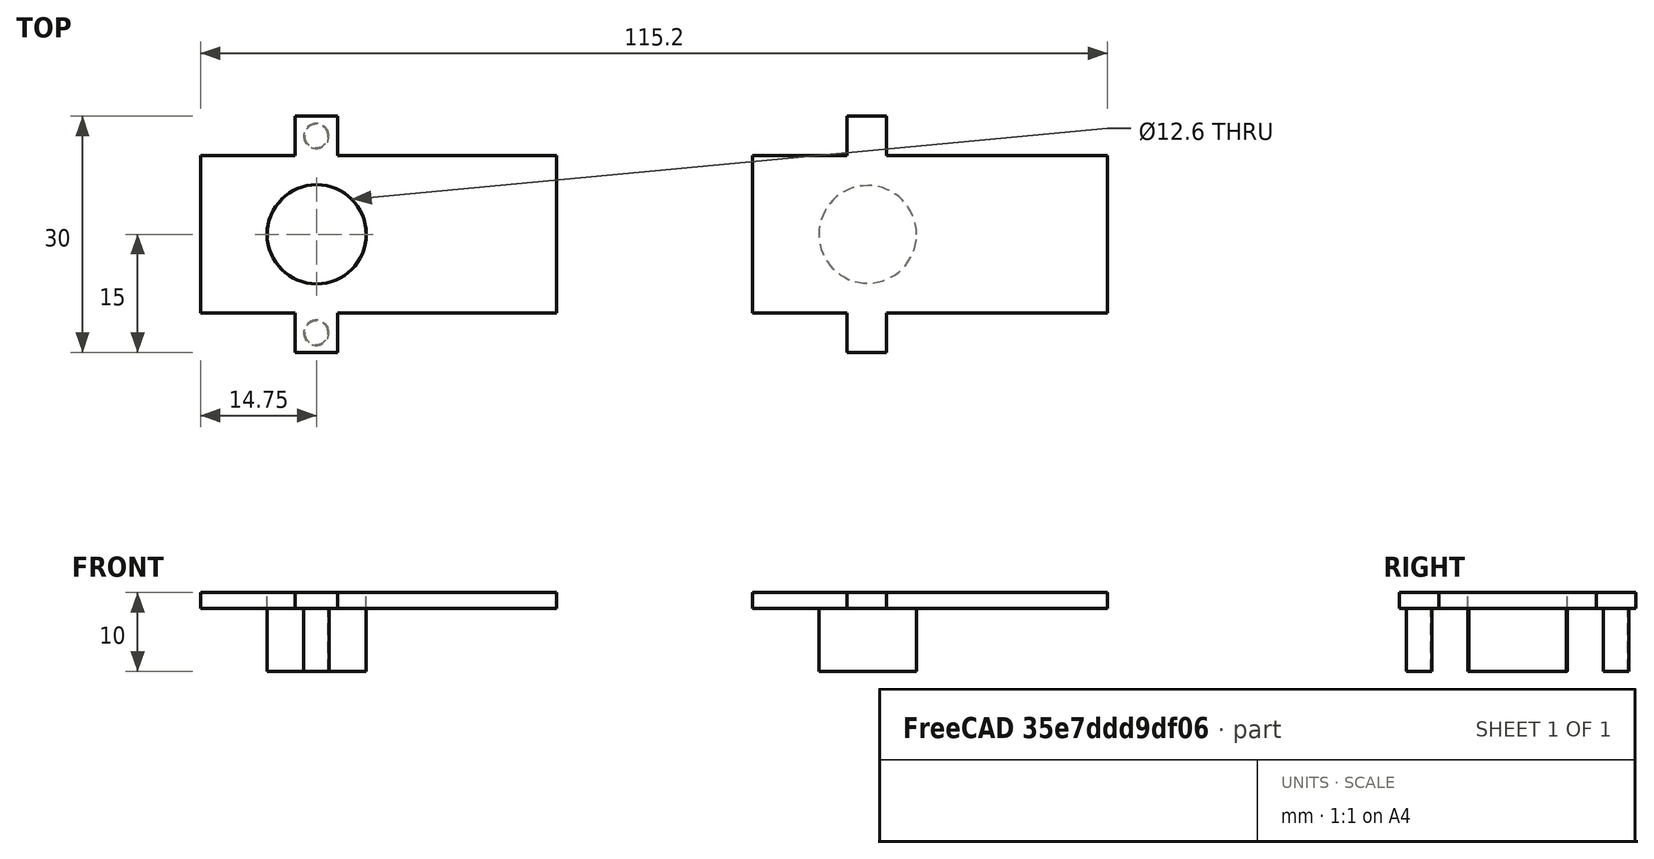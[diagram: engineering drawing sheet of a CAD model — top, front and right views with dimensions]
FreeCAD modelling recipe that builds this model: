
FCSTD DOCUMENT  (FreeCAD 0.18R16110 (Git))
Label: ccortador_encoder_doble
License: All rights reserved
LicenseURL: http://en.wikipedia.org/wiki/All_rights_reserved
objects: Part::Box×6, Part::Cylinder×4, Part::Fuse×4, Part::MultiFuse×3, Part::FeaturePython×1, Part::Feature×1
note: 19 computed .brp shape members not serialized (recipe doc carries the construction recipe); baked Part::Feature solids carry a one-line shape summary decoded from their .brp

FEATURE [Part::Cylinder] Cylinder  label="taladro1"
  Angle = 360
  AttacherType = Attacher::AttachEngine3D
  Height = 10
  Placement = pos=(-7.9,-12.5,-6) rot=(0,0,1;0rad)
  Radius = 1.6
FEATURE [Part::Cylinder] Cylinder001  label="taladro2"
  Angle = 360
  AttacherType = Attacher::AttachEngine3D
  Height = 10
  Placement = pos=(-7.9,12.5,-6) rot=(0,0,1;0rad)
  Radius = 1.6
FEATURE [Part::Box] Box  label="base"
  AttacherType = Attacher::AttachEngine3D
  Height = 2
  Length = 45.2
  Placement = pos=(-22.6,-10,2) rot=(0,0,1;0rad)
  Width = 20
FEATURE [Part::Box] Box001  label="oreja2"
  AttacherType = Attacher::AttachEngine3D
  Height = 2
  Length = 5.4
  Placement = pos=(-10.6,10,2) rot=(0,0,1;0rad)
  Width = 5
FEATURE [Part::Box] Box002  label="oreja1"
  AttacherType = Attacher::AttachEngine3D
  Height = 2
  Length = 5.4
  Placement = pos=(-10.6,-15,2) rot=(0,0,1;0rad)
  Width = 5
FEATURE [Part::Fuse] Fusion
  Base = -> Box
  Tool = -> Box002
FEATURE [Part::Fuse] Fusion001
  Base = -> Box001
  Tool = -> Fusion
FEATURE [Part::Fuse] Fusion002
  Base = -> Cylinder
  Tool = -> Fusion001
FEATURE [Part::Fuse] Fusion003  label="posicionador encoder doble"
  Base = -> Cylinder001
  Placement = pos=(0,0,-4) rot=(0,0,1;0rad)
  Tool = -> Fusion002
FEATURE [Part::Cylinder] Cylinder002  label="engranaje-bastago-grande"
  Angle = 360
  AttacherType = Attacher::AttachEngine3D
  Height = 10
  Placement = pos=(-7.85,0,-10) rot=(0,0,1;0rad)
  Radius = 6.3
FEATURE [Part::FeaturePython] BooleanFragments  label="posicion_encoder_doble"  # WARN: FeaturePython — macro-defined, semantics opaque (R4)
  Mode = 0
  Objects = -> [Fusion003,Cylinder002]
  Tolerance = 0
FEATURE [Part::Feature] BooleanFragments_solid  label="posicion_encoder_doble (Solid)"
  shape: bbox 45.2 x 30 x 10 mm, 29 faces (baked)
FEATURE [Part::Box] Box004  label="Cube001"
  AttacherType = Attacher::AttachEngine3D
  Height = 2
  Length = 5
  Placement = pos=(59.5,-15,-2) rot=(0,0,1;0rad)
  Width = 5
FEATURE [Part::Box] Box005  label="Cube002"
  AttacherType = Attacher::AttachEngine3D
  Height = 2
  Length = 5
  Placement = pos=(59.5,10,-2) rot=(0,0,1;0rad)
  Width = 5
FEATURE [Part::Box] Box006  label="Cube003"
  AttacherType = Attacher::AttachEngine3D
  Height = 2
  Length = 45.1
  Placement = pos=(47.5,-10,-2) rot=(0,0,1;0rad)
  Width = 20
FEATURE [Part::MultiFuse] Fusion004
  Shapes = -> [Box004,Box005]
FEATURE [Part::MultiFuse] Fusion005
  Shapes = -> [Fusion004,Box006]
FEATURE [Part::Cylinder] Cylinder003  label="Cylinder"
  Angle = 360
  AttacherType = Attacher::AttachEngine3D
  Height = 10
  Placement = pos=(62.15,0,-10) rot=(0,0,1;0rad)
  Radius = 6.2
FEATURE [Part::MultiFuse] Fusion006  label="corta_cilindo_solo"
  Shapes = -> [Fusion005,Cylinder003]
